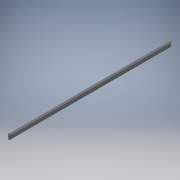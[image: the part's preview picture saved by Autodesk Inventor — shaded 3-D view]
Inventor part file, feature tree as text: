
AUTODESK INVENTOR PART (.ipt)
format: ipt  version: 2017.1 (Build 211199000, 199)  size: 118,784 bytes
history: native  units: in
note: dims shown in document units (in); Inventor stores cm internally (conversion verified against a paired STEP export)
features: fillet x1, other x1, imported_body x1
ambient origin geometry x8: Origin, YZ Plane, XZ Plane, XY Plane, X Axis, Y Axis, Z Axis, Center Point
bodies: Body1 (feature_tree)
feature tree (3):
  fillet  "Fillet1"  [1 undecoded]
  other  "BWC-T1-11"
  imported_body  "Base1"
note: 1 required parameter value undecoded (feature->parameter linkage not recoverable at this tier; creation-order binding heuristic only, values carry confidence <= 0.55)
